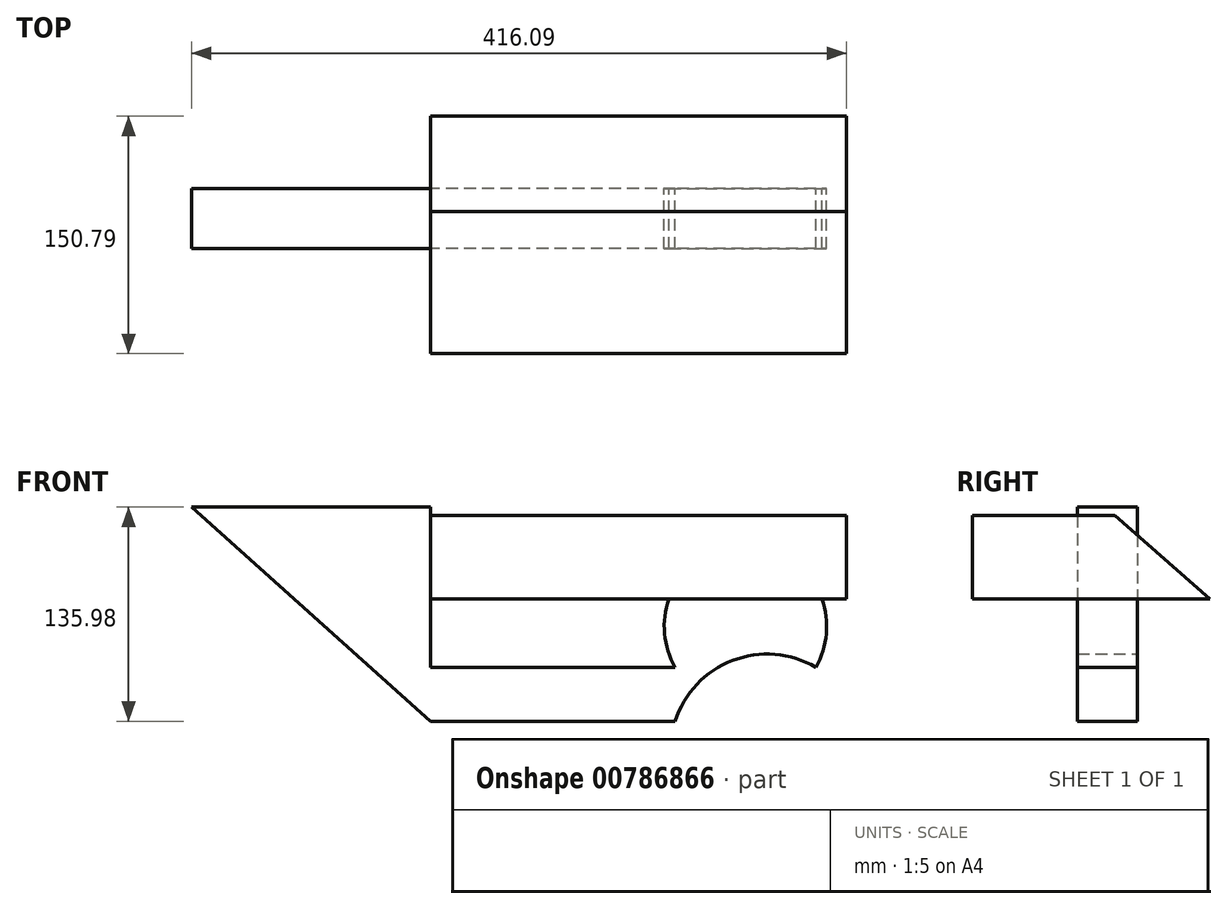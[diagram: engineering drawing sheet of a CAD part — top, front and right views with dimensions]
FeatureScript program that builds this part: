
annotation { "Feature Type Name" : "Feature", "Feature Type Description" : "" }
export const myFeature = defineFeature(function(context is Context, id is Id, definition is map)
    precondition{}
    {
        {
            var Q0;
            Q0=qCreatedBy(makeId("Front.planeOp"),FACE);
            var sketch = newSketch(context, id + "F0", { "sketchPlane" : qUnion([Q0])});
            skLineSegment(sketch, "E0", {"start": v(-151.93, 101.65) * mm, "end": v(0, 101.65) * mm});
            skLineSegment(sketch, "E1", {"start": v(0, 101.65) * mm, "end": v(0, 0) * mm});
            skLineSegment(sketch, "E2", {"start": v(0, 0) * mm, "end": v(155.23, 0) * mm});
            skArc(sketch, "E3", {"start": v(244.62, 0) * mm, "mid": v(199.92, 77.34) * mm, "end": v(155.23, 0) * mm});
            skArc(sketch, "E4", {"start": v(244.62, 0) * mm, "mid": v(191.7, 4.22) * mm, "end": v(155.23, -34.33) * mm});
            skLineSegment(sketch, "E5", {"start": v(155.23, -34.33) * mm, "end": v(0, -34.33) * mm});
            skLineSegment(sketch, "E6", {"start": v(0, -34.33) * mm, "end": v(-151.93, 101.65) * mm});
            skSolve(sketch);
        }
        {
            var Q0;
            Q0=makeQuery(id+"F0.imprint","IMPRINT",FACE,{"disambiguationData":[TD([[makeQuery(id+"F0.imprint","IMPRINT",EDGE,{"derivedFrom":sQuery(id+"F0.wireOp",EDGE,"E0")}),-1.0]])]});
            extrude(context, id + "F1", {"entities" : qUnion([Q0]), "depth" : 38.1 * mm, "offsetDistance" : 25.4 * mm});
        }
        {
            var Q0;
            Q0=qCreatedBy(makeId("Right.planeOp"),FACE);
            var sketch = newSketch(context, id + "F2", { "sketchPlane" : qUnion([Q0])});
            skLineSegment(sketch, "E7", {"start": v(-104.76, 96.36) * mm, "end": v(-14.35, 96.36) * mm});
            skLineSegment(sketch, "E8", {"start": v(-14.35, 96.36) * mm, "end": v(46.03, 43.25) * mm});
            skLineSegment(sketch, "E9", {"start": v(46.03, 43.25) * mm, "end": v(-104.76, 43.25) * mm});
            skLineSegment(sketch, "E10", {"start": v(-104.76, 43.25) * mm, "end": v(-104.76, 96.36) * mm});
            skSolve(sketch);
        }
        {
            var Q0;
            Q0=makeQuery(id+"F2.imprint","IMPRINT",FACE,{"disambiguationData":[TD([[makeQuery(id+"F2.imprint","IMPRINT",EDGE,{"derivedFrom":sQuery(id+"F2.wireOp",EDGE,"E7")}),-1.0]])]});
            extrude(context, id + "F3", {"entities" : qUnion([Q0]), "operationType" : NewBodyOperationType.ADD, "depth" : 264.16 * mm, "offsetDistance" : 25.4 * mm});
        }
    });
